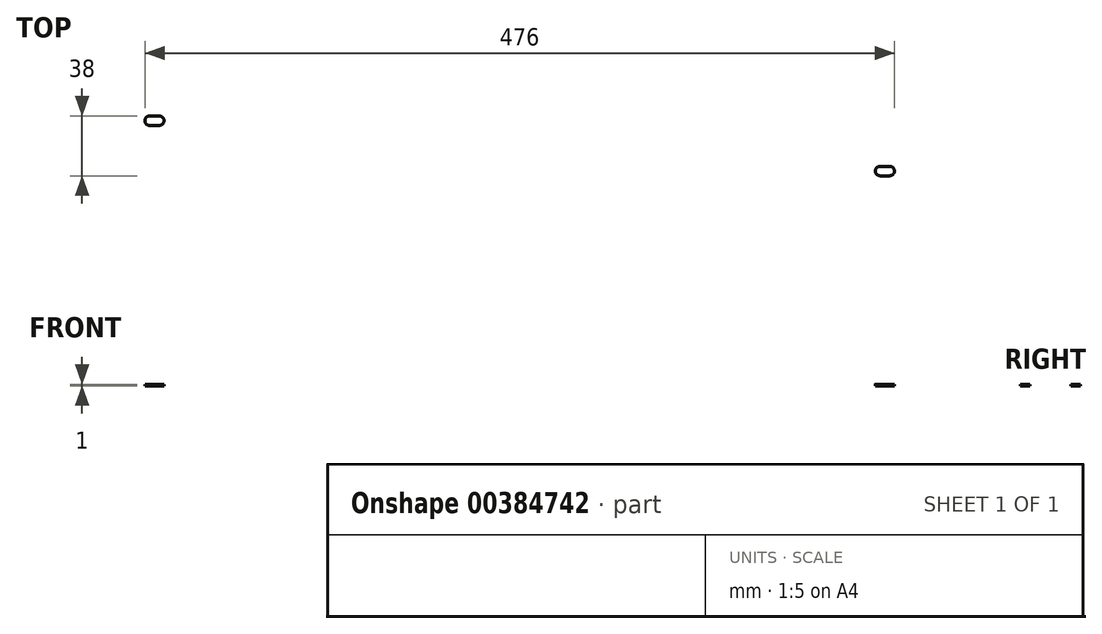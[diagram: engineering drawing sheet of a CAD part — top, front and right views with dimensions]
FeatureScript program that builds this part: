
annotation { "Feature Type Name" : "Feature", "Feature Type Description" : "" }
export const myFeature = defineFeature(function(context is Context, id is Id, definition is map)
    precondition{}
    {
        {
            var Q0;
            Q0=qCreatedBy(makeId("Top.planeOp"),FACE);
            var sketch = newSketch(context, id + "F0", { "sketchPlane" : qUnion([Q0])});
            skLineSegment(sketch, "E0.right", {"start": v(221, 33.5) * mm, "end": v(221, 20) * mm});
            skLineSegment(sketch, "E1", {"start": v(239, 22) * mm, "end": v(241, 20) * mm});
            skLineSegment(sketch, "E2", {"start": v(239, 22) * mm, "end": v(223, 22) * mm});
            skLineSegment(sketch, "E3", {"start": v(223, 22) * mm, "end": v(223, 20) * mm});
            skLineSegment(sketch, "E4", {"start": v(221, 20) * mm, "end": v(221, 33.5) * mm});
            skLineSegment(sketch, "E5", {"start": v(223, 20) * mm, "end": v(221, 20) * mm});
            skLineSegment(sketch, "E6", {"start": v(221, 33.5) * mm, "end": v(0, 33.5) * mm});
            skLineSegment(sketch, "E7", {"start": v(241, 20) * mm, "end": v(241, 0) * mm});
            skLineSegment(sketch, "E8.MirrorCS", {"start": v(-223, 20) * mm, "end": v(-221, 20) * mm});
            skLineSegment(sketch, "E9.MirrorCS", {"start": v(-223, 22) * mm, "end": v(-223, 20) * mm});
            skLineSegment(sketch, "E10.MirrorCS", {"start": v(-239, 22) * mm, "end": v(-241, 20) * mm});
            skLineSegment(sketch, "E11.MirrorCS", {"start": v(-221, 33.5) * mm, "end": v(-221, 20) * mm});
            skLineSegment(sketch, "E12.MirrorCS", {"start": v(-221, 33.5) * mm, "end": v(0, 33.5) * mm});
            skLineSegment(sketch, "E13.MirrorCS", {"start": v(-239, 22) * mm, "end": v(-223, 22) * mm});
            skLineSegment(sketch, "E14.MirrorCS", {"start": v(-241, 20) * mm, "end": v(-241, 0) * mm});
            skLineSegment(sketch, "E15.MirrorCS", {"start": v(-221, 20) * mm, "end": v(-221, 33.5) * mm});
            skLineSegment(sketch, "E16.MirrorCS", {"start": v(223, -22) * mm, "end": v(223, -20) * mm});
            skLineSegment(sketch, "E17.MirrorCS", {"start": v(-223, -22) * mm, "end": v(-223, -20) * mm});
            skLineSegment(sketch, "E18.MirrorCS", {"start": v(223, -20) * mm, "end": v(221, -20) * mm});
            skLineSegment(sketch, "E19.MirrorCS", {"start": v(-223, -20) * mm, "end": v(-221, -20) * mm});
            skLineSegment(sketch, "E20.MirrorCS", {"start": v(221, -20) * mm, "end": v(221, -33.5) * mm});
            skLineSegment(sketch, "E21.MirrorCS", {"start": v(-221, -33.5) * mm, "end": v(-221, -20) * mm});
            skLineSegment(sketch, "E22.MirrorCS", {"start": v(221, -33.5) * mm, "end": v(221, -20) * mm});
            skLineSegment(sketch, "E23.MirrorCS", {"start": v(-221, -20) * mm, "end": v(-221, -33.5) * mm});
            skLineSegment(sketch, "E24.MirrorCS", {"start": v(-239, -22) * mm, "end": v(-241, -20) * mm});
            skLineSegment(sketch, "E25.MirrorCS", {"start": v(-239, -22) * mm, "end": v(-223, -22) * mm});
            skLineSegment(sketch, "E26.MirrorCS", {"start": v(239, -22) * mm, "end": v(241, -20) * mm});
            skLineSegment(sketch, "E27.MirrorCS", {"start": v(239, -22) * mm, "end": v(223, -22) * mm});
            skLineSegment(sketch, "E28.MirrorCS", {"start": v(-241, -20) * mm, "end": v(-241, 0) * mm});
            skLineSegment(sketch, "E29.MirrorCS", {"start": v(241, -20) * mm, "end": v(241, 0) * mm});
            skLineSegment(sketch, "E30.MirrorCS", {"start": v(-221, -33.5) * mm, "end": v(0, -33.5) * mm});
            skLineSegment(sketch, "E31.MirrorCS", {"start": v(221, -33.5) * mm, "end": v(0, -33.5) * mm});
            skSolve(sketch);
        }
        {
            var Q0;
            Q0=makeQuery(id+"F0.imprint","IMPRINT",FACE,{"disambiguationData":[TD([[makeQuery(id+"F0.imprint","IMPRINT",EDGE,{"derivedFrom":sQuery(id+"F0.wireOp",EDGE,"E8.MirrorCS")}),-1.0]])]});
            extrude(context, id + "F1", {"entities" : qUnion([Q0]), "depth" : 1 * mm});
        }
        {
            var Q0;
            Q0=makeQuery(id+"F1.opExtrude","CAP_FACE",FACE,{"disambiguationData":[OSD([sQuery(id+"F0.wireOp",EDGE,"E8.MirrorCS"),sQuery(id+"F0.wireOp",EDGE,"E9.MirrorCS"),sQuery(id+"F0.wireOp",EDGE,"E11.MirrorCS"),sQuery(id+"F0.wireOp",EDGE,"E5"),sQuery(id+"F0.wireOp",EDGE,"E3"),sQuery(id+"F0.wireOp",EDGE,"E0.right"),sQuery(id+"F0.wireOp",EDGE,"E10.MirrorCS"),sQuery(id+"F0.wireOp",EDGE,"E2"),sQuery(id+"F0.wireOp",EDGE,"E13.MirrorCS"),sQuery(id+"F0.wireOp",EDGE,"E1"),sQuery(id+"F0.wireOp",EDGE,"E14.MirrorCS"),sQuery(id+"F0.wireOp",EDGE,"E7"),sQuery(id+"F0.wireOp",EDGE,"E6"),sQuery(id+"F0.wireOp",EDGE,"E12.MirrorCS"),sQuery(id+"F0.wireOp",EDGE,"E17.MirrorCS"),sQuery(id+"F0.wireOp",EDGE,"E16.MirrorCS"),sQuery(id+"F0.wireOp",EDGE,"E19.MirrorCS"),sQuery(id+"F0.wireOp",EDGE,"E18.MirrorCS"),sQuery(id+"F0.wireOp",EDGE,"E22.MirrorCS"),sQuery(id+"F0.wireOp",EDGE,"E23.MirrorCS"),sQuery(id+"F0.wireOp",EDGE,"E24.MirrorCS"),sQuery(id+"F0.wireOp",EDGE,"E25.MirrorCS"),sQuery(id+"F0.wireOp",EDGE,"E27.MirrorCS"),sQuery(id+"F0.wireOp",EDGE,"E26.MirrorCS"),sQuery(id+"F0.wireOp",EDGE,"E28.MirrorCS"),sQuery(id+"F0.wireOp",EDGE,"E29.MirrorCS"),sQuery(id+"F0.wireOp",EDGE,"E31.MirrorCS"),sQuery(id+"F0.wireOp",EDGE,"E30.MirrorCS")])],"isStart":false});
            var sketch = newSketch(context, id + "F2", { "sketchPlane" : qUnion([Q0])});
            skPoint(sketch, "E32", {"position": v(-200, 0) * mm});
            skPoint(sketch, "E33", {"position": v(-100, 0) * mm});
            skPoint(sketch, "E34", {"position": v(0, 0) * mm});
            skPoint(sketch, "E35", {"position": v(100, 0) * mm});
            skPoint(sketch, "E36", {"position": v(200, 0) * mm});
            skSolve(sketch);
        }
        {
            var Q0;
            Q0=sQuery(id+"F2.wireOp",VERTEX,"E32");
            var Q1;
            Q1=sQuery(id+"F2.wireOp",VERTEX,"E33");
            var Q2;
            Q2=sQuery(id+"F2.wireOp",VERTEX,"E34");
            var Q3;
            Q3=sQuery(id+"F2.wireOp",VERTEX,"E35");
            var Q4;
            Q4=sQuery(id+"F2.wireOp",VERTEX,"E36");
            var Q5;
            Q5=makeQuery(id+"F1.opExtrude","SWEPT_BODY",BODY,{"disambiguationData":[OSD([sQuery(id+"F0.wireOp",EDGE,"E8.MirrorCS"),sQuery(id+"F0.wireOp",EDGE,"E9.MirrorCS"),sQuery(id+"F0.wireOp",EDGE,"E11.MirrorCS"),sQuery(id+"F0.wireOp",EDGE,"E5"),sQuery(id+"F0.wireOp",EDGE,"E3"),sQuery(id+"F0.wireOp",EDGE,"E0.right"),sQuery(id+"F0.wireOp",EDGE,"E10.MirrorCS"),sQuery(id+"F0.wireOp",EDGE,"E2"),sQuery(id+"F0.wireOp",EDGE,"E13.MirrorCS"),sQuery(id+"F0.wireOp",EDGE,"E1"),sQuery(id+"F0.wireOp",EDGE,"E14.MirrorCS"),sQuery(id+"F0.wireOp",EDGE,"E7"),sQuery(id+"F0.wireOp",EDGE,"E6"),sQuery(id+"F0.wireOp",EDGE,"E12.MirrorCS"),sQuery(id+"F0.wireOp",EDGE,"E17.MirrorCS"),sQuery(id+"F0.wireOp",EDGE,"E16.MirrorCS"),sQuery(id+"F0.wireOp",EDGE,"E19.MirrorCS"),sQuery(id+"F0.wireOp",EDGE,"E18.MirrorCS"),sQuery(id+"F0.wireOp",EDGE,"E22.MirrorCS"),sQuery(id+"F0.wireOp",EDGE,"E23.MirrorCS"),sQuery(id+"F0.wireOp",EDGE,"E24.MirrorCS"),sQuery(id+"F0.wireOp",EDGE,"E25.MirrorCS"),sQuery(id+"F0.wireOp",EDGE,"E27.MirrorCS"),sQuery(id+"F0.wireOp",EDGE,"E26.MirrorCS"),sQuery(id+"F0.wireOp",EDGE,"E28.MirrorCS"),sQuery(id+"F0.wireOp",EDGE,"E29.MirrorCS"),sQuery(id+"F0.wireOp",EDGE,"E31.MirrorCS"),sQuery(id+"F0.wireOp",EDGE,"E30.MirrorCS")])]});
            hole(context, id + "F3", {"style" : HoleStyle.SIMPLE, "endStyle" : HoleEndStyle.THROUGH, "holeDiameter" : 5 * mm, "isTappedThrough" : true, "tappedDepth" : 12 * mm, "tapClearance" : 3, "locations" : qUnion([Q0, Q1, Q2, Q3, Q4]), "scope" : qUnion([Q5])});
        }
        {
            var Q0;
            Q0=makeQuery(id+"F1.opExtrude","CAP_FACE",FACE,{"disambiguationData":[OSD([sQuery(id+"F0.wireOp",EDGE,"E8.MirrorCS"),sQuery(id+"F0.wireOp",EDGE,"E9.MirrorCS"),sQuery(id+"F0.wireOp",EDGE,"E11.MirrorCS"),sQuery(id+"F0.wireOp",EDGE,"E5"),sQuery(id+"F0.wireOp",EDGE,"E3"),sQuery(id+"F0.wireOp",EDGE,"E0.right"),sQuery(id+"F0.wireOp",EDGE,"E10.MirrorCS"),sQuery(id+"F0.wireOp",EDGE,"E2"),sQuery(id+"F0.wireOp",EDGE,"E13.MirrorCS"),sQuery(id+"F0.wireOp",EDGE,"E1"),sQuery(id+"F0.wireOp",EDGE,"E14.MirrorCS"),sQuery(id+"F0.wireOp",EDGE,"E7"),sQuery(id+"F0.wireOp",EDGE,"E6"),sQuery(id+"F0.wireOp",EDGE,"E12.MirrorCS"),sQuery(id+"F0.wireOp",EDGE,"E17.MirrorCS"),sQuery(id+"F0.wireOp",EDGE,"E16.MirrorCS"),sQuery(id+"F0.wireOp",EDGE,"E19.MirrorCS"),sQuery(id+"F0.wireOp",EDGE,"E18.MirrorCS"),sQuery(id+"F0.wireOp",EDGE,"E22.MirrorCS"),sQuery(id+"F0.wireOp",EDGE,"E23.MirrorCS"),sQuery(id+"F0.wireOp",EDGE,"E24.MirrorCS"),sQuery(id+"F0.wireOp",EDGE,"E25.MirrorCS"),sQuery(id+"F0.wireOp",EDGE,"E27.MirrorCS"),sQuery(id+"F0.wireOp",EDGE,"E26.MirrorCS"),sQuery(id+"F0.wireOp",EDGE,"E28.MirrorCS"),sQuery(id+"F0.wireOp",EDGE,"E29.MirrorCS"),sQuery(id+"F0.wireOp",EDGE,"E31.MirrorCS"),sQuery(id+"F0.wireOp",EDGE,"E30.MirrorCS")])],"isStart":false});
            var sketch = newSketch(context, id + "F4", { "sketchPlane" : qUnion([Q0])});
            skPoint(sketch, "E37.MirrorP", {"position": v(-228.9, -16) * mm});
            skPoint(sketch, "E38.MirrorP", {"position": v(-235, -16) * mm});
            skArc(sketch, "E39", {"start": v(-235, -13) * mm, "mid": v(-238, -16) * mm, "end": v(-235, -19) * mm});
            skArc(sketch, "E40", {"start": v(-228.9, -19) * mm, "mid": v(-225.9, -16) * mm, "end": v(-228.9, -13) * mm});
            skLineSegment(sketch, "E41", {"start": v(-235, -13) * mm, "end": v(-228.9, -13) * mm});
            skLineSegment(sketch, "E42", {"start": v(-228.9, -19) * mm, "end": v(-235, -19) * mm});
            skPoint(sketch, "E43.MirrorP", {"position": v(235, -16) * mm});
            skPoint(sketch, "E44.MirrorP", {"position": v(228.9, -16) * mm});
            skArc(sketch, "E45.MirrorCS", {"start": v(228.9, -19) * mm, "mid": v(225.9, -16) * mm, "end": v(228.9, -13) * mm});
            skLineSegment(sketch, "E46.MirrorCS", {"start": v(235, -13) * mm, "end": v(228.9, -13) * mm});
            skLineSegment(sketch, "E47.MirrorCS", {"start": v(228.9, -19) * mm, "end": v(235, -19) * mm});
            skArc(sketch, "E48.MirrorCS", {"start": v(235, -13) * mm, "mid": v(238, -16) * mm, "end": v(235, -19) * mm});
            skArc(sketch, "E49.MirrorCS", {"start": v(-235, 13) * mm, "mid": v(-238, 16) * mm, "end": v(-235, 19) * mm});
            skLineSegment(sketch, "E50.MirrorCS", {"start": v(-235, 13) * mm, "end": v(-228.9, 13) * mm});
            skArc(sketch, "E51.MirrorCS", {"start": v(-228.9, 19) * mm, "mid": v(-225.9, 16) * mm, "end": v(-228.9, 13) * mm});
            skLineSegment(sketch, "E52.MirrorCS", {"start": v(-228.9, 19) * mm, "end": v(-235, 19) * mm});
            skLineSegment(sketch, "E53.MirrorCS", {"start": v(235, 13) * mm, "end": v(228.9, 13) * mm});
            skLineSegment(sketch, "E54.MirrorCS", {"start": v(228.9, 19) * mm, "end": v(235, 19) * mm});
            skArc(sketch, "E55.MirrorCS", {"start": v(228.9, 19) * mm, "mid": v(225.9, 16) * mm, "end": v(228.9, 13) * mm});
            skArc(sketch, "E56.MirrorCS", {"start": v(235, 13) * mm, "mid": v(238, 16) * mm, "end": v(235, 19) * mm});
            skSolve(sketch);
        }
        {
            var Q0;
            Q0=makeQuery(id+"F4.imprint","IMPRINT",FACE,{"disambiguationData":[TD([[makeQuery(id+"F4.imprint","IMPRINT",EDGE,{"derivedFrom":sQuery(id+"F4.wireOp",EDGE,"E39")}),1.0]])]});
            var Q1;
            Q1=makeQuery(id+"F4.imprint","IMPRINT",FACE,{"disambiguationData":[TD([[makeQuery(id+"F4.imprint","IMPRINT",EDGE,{"derivedFrom":sQuery(id+"F4.wireOp",EDGE,"E49.MirrorCS")}),-1.0]])]});
            var Q2;
            Q2=makeQuery(id+"F4.imprint","IMPRINT",FACE,{"disambiguationData":[TD([[makeQuery(id+"F4.imprint","IMPRINT",EDGE,{"derivedFrom":sQuery(id+"F4.wireOp",EDGE,"E53.MirrorCS")}),-1.0]])]});
            var Q3;
            Q3=makeQuery(id+"F4.imprint","IMPRINT",FACE,{"disambiguationData":[TD([[makeQuery(id+"F4.imprint","IMPRINT",EDGE,{"derivedFrom":sQuery(id+"F4.wireOp",EDGE,"E45.MirrorCS")}),-1.0]])]});
            extrude(context, id + "F5", {"entities" : qUnion([Q0, Q1, Q2, Q3]), "operationType" : NewBodyOperationType.REMOVE, "oppositeDirection" : true, "depth" : 25 * mm});
        }
        {
            var Q0;
            Q0=makeQuery(id+"F1.opExtrude","CAP_FACE",FACE,{"disambiguationData":[OSD([sQuery(id+"F0.wireOp",EDGE,"E8.MirrorCS"),sQuery(id+"F0.wireOp",EDGE,"E9.MirrorCS"),sQuery(id+"F0.wireOp",EDGE,"E11.MirrorCS"),sQuery(id+"F0.wireOp",EDGE,"E5"),sQuery(id+"F0.wireOp",EDGE,"E3"),sQuery(id+"F0.wireOp",EDGE,"E0.right"),sQuery(id+"F0.wireOp",EDGE,"E10.MirrorCS"),sQuery(id+"F0.wireOp",EDGE,"E2"),sQuery(id+"F0.wireOp",EDGE,"E13.MirrorCS"),sQuery(id+"F0.wireOp",EDGE,"E1"),sQuery(id+"F0.wireOp",EDGE,"E14.MirrorCS"),sQuery(id+"F0.wireOp",EDGE,"E7"),sQuery(id+"F0.wireOp",EDGE,"E6"),sQuery(id+"F0.wireOp",EDGE,"E12.MirrorCS"),sQuery(id+"F0.wireOp",EDGE,"E17.MirrorCS"),sQuery(id+"F0.wireOp",EDGE,"E16.MirrorCS"),sQuery(id+"F0.wireOp",EDGE,"E19.MirrorCS"),sQuery(id+"F0.wireOp",EDGE,"E18.MirrorCS"),sQuery(id+"F0.wireOp",EDGE,"E22.MirrorCS"),sQuery(id+"F0.wireOp",EDGE,"E23.MirrorCS"),sQuery(id+"F0.wireOp",EDGE,"E24.MirrorCS"),sQuery(id+"F0.wireOp",EDGE,"E25.MirrorCS"),sQuery(id+"F0.wireOp",EDGE,"E27.MirrorCS"),sQuery(id+"F0.wireOp",EDGE,"E26.MirrorCS"),sQuery(id+"F0.wireOp",EDGE,"E28.MirrorCS"),sQuery(id+"F0.wireOp",EDGE,"E29.MirrorCS"),sQuery(id+"F0.wireOp",EDGE,"E31.MirrorCS"),sQuery(id+"F0.wireOp",EDGE,"E30.MirrorCS")])],"isStart":true});
            var sketch = newSketch(context, id + "F6", { "sketchPlane" : qUnion([Q0])});
            skLineSegment(sketch, "E57.bottom", {"start": v(-120, 12) * mm, "end": v(-180, 12) * mm});
            skLineSegment(sketch, "E57.top", {"start": v(-120, -12) * mm, "end": v(-180, -12) * mm});
            skLineSegment(sketch, "E57.left", {"start": v(-115, 7) * mm, "end": v(-115, -7) * mm});
            skLineSegment(sketch, "E57.right", {"start": v(-185, 7) * mm, "end": v(-185, -7) * mm});
            skPoint(sketch, "E57.middle", {"position": v(-150, 0) * mm});
            skPoint(sketch, "E58.visualSharp", {"position": v(-115, 12) * mm});
            skArc(sketch, "E58.filletArc", {"start": v(-115, 7) * mm, "mid": v(-116.46, 10.54) * mm, "end": v(-120, 12) * mm});
            skPoint(sketch, "E59.visualSharp", {"position": v(-185, 12) * mm});
            skArc(sketch, "E59.filletArc", {"start": v(-180, 12) * mm, "mid": v(-183.54, 10.54) * mm, "end": v(-185, 7) * mm});
            skPoint(sketch, "E60.visualSharp", {"position": v(-185, -12) * mm});
            skArc(sketch, "E60.filletArc", {"start": v(-185, -7) * mm, "mid": v(-183.54, -10.54) * mm, "end": v(-180, -12) * mm});
            skPoint(sketch, "E61.visualSharp", {"position": v(-115, -12) * mm});
            skArc(sketch, "E61.filletArc", {"start": v(-120, -12) * mm, "mid": v(-116.46, -10.54) * mm, "end": v(-115, -7) * mm});
            skLineSegment(sketch, "E62.bottom", {"start": v(-20, 12) * mm, "end": v(-80, 12) * mm});
            skLineSegment(sketch, "E62.top", {"start": v(-20, -12) * mm, "end": v(-80, -12) * mm});
            skLineSegment(sketch, "E62.left", {"start": v(-15, 7) * mm, "end": v(-15, -7) * mm});
            skLineSegment(sketch, "E62.right", {"start": v(-85, 7) * mm, "end": v(-85, -7) * mm});
            skPoint(sketch, "E62.middle", {"position": v(-50, 0) * mm});
            skPoint(sketch, "E63.visualSharp", {"position": v(-15, 12) * mm});
            skArc(sketch, "E63.filletArc", {"start": v(-15, 7) * mm, "mid": v(-16.46, 10.54) * mm, "end": v(-20, 12) * mm});
            skPoint(sketch, "E64.visualSharp", {"position": v(-85, 12) * mm});
            skArc(sketch, "E64.filletArc", {"start": v(-80, 12) * mm, "mid": v(-83.54, 10.54) * mm, "end": v(-85, 7) * mm});
            skPoint(sketch, "E65.visualSharp", {"position": v(-85, -12) * mm});
            skArc(sketch, "E65.filletArc", {"start": v(-85, -7) * mm, "mid": v(-83.54, -10.54) * mm, "end": v(-80, -12) * mm});
            skPoint(sketch, "E66.visualSharp", {"position": v(-15, -12) * mm});
            skArc(sketch, "E66.filletArc", {"start": v(-20, -12) * mm, "mid": v(-16.46, -10.54) * mm, "end": v(-15, -7) * mm});
            skArc(sketch, "E67.MirrorCS", {"start": v(15, 7) * mm, "mid": v(16.46, 10.54) * mm, "end": v(20, 12) * mm});
            skArc(sketch, "E68.MirrorCS", {"start": v(80, 12) * mm, "mid": v(83.54, 10.54) * mm, "end": v(85, 7) * mm});
            skArc(sketch, "E69.MirrorCS", {"start": v(85, -7) * mm, "mid": v(83.54, -10.54) * mm, "end": v(80, -12) * mm});
            skArc(sketch, "E70.MirrorCS", {"start": v(20, -12) * mm, "mid": v(16.46, -10.54) * mm, "end": v(15, -7) * mm});
            skArc(sketch, "E71.MirrorCS", {"start": v(115, 7) * mm, "mid": v(116.46, 10.54) * mm, "end": v(120, 12) * mm});
            skArc(sketch, "E72.MirrorCS", {"start": v(180, 12) * mm, "mid": v(183.54, 10.54) * mm, "end": v(185, 7) * mm});
            skArc(sketch, "E73.MirrorCS", {"start": v(185, -7) * mm, "mid": v(183.54, -10.54) * mm, "end": v(180, -12) * mm});
            skArc(sketch, "E74.MirrorCS", {"start": v(120, -12) * mm, "mid": v(116.46, -10.54) * mm, "end": v(115, -7) * mm});
            skPoint(sketch, "E75.MirrorP", {"position": v(185, 12) * mm});
            skPoint(sketch, "E76.MirrorP", {"position": v(150, 0) * mm});
            skPoint(sketch, "E77.MirrorP", {"position": v(15, -12) * mm});
            skPoint(sketch, "E78.MirrorP", {"position": v(15, 12) * mm});
            skPoint(sketch, "E79.MirrorP", {"position": v(115, -12) * mm});
            skPoint(sketch, "E80.MirrorP", {"position": v(115, 12) * mm});
            skPoint(sketch, "E81.MirrorP", {"position": v(50, 0) * mm});
            skPoint(sketch, "E82.MirrorP", {"position": v(85, 12) * mm});
            skPoint(sketch, "E83.MirrorP", {"position": v(85, -12) * mm});
            skLineSegment(sketch, "E84.MirrorCS", {"start": v(85, 7) * mm, "end": v(85, -7) * mm});
            skLineSegment(sketch, "E85.MirrorCS", {"start": v(15, 7) * mm, "end": v(15, -7) * mm});
            skLineSegment(sketch, "E86.MirrorCS", {"start": v(120, 12) * mm, "end": v(180, 12) * mm});
            skLineSegment(sketch, "E87.MirrorCS", {"start": v(120, -12) * mm, "end": v(180, -12) * mm});
            skLineSegment(sketch, "E88.MirrorCS", {"start": v(115, 7) * mm, "end": v(115, -7) * mm});
            skLineSegment(sketch, "E89.MirrorCS", {"start": v(185, 7) * mm, "end": v(185, -7) * mm});
            skPoint(sketch, "E90.MirrorP", {"position": v(185, -12) * mm});
            skLineSegment(sketch, "E91.MirrorCS", {"start": v(20, 12) * mm, "end": v(80, 12) * mm});
            skLineSegment(sketch, "E92.MirrorCS", {"start": v(20, -12) * mm, "end": v(80, -12) * mm});
            skSolve(sketch);
        }
        {
            var Q0;
            Q0=makeQuery(id+"F6.imprint","IMPRINT",FACE,{"disambiguationData":[TD([[makeQuery(id+"F6.imprint","IMPRINT",EDGE,{"derivedFrom":sQuery(id+"F6.wireOp",EDGE,"E71.MirrorCS")}),-1.0]])]});
            var Q1;
            Q1=makeQuery(id+"F6.imprint","IMPRINT",FACE,{"disambiguationData":[TD([[makeQuery(id+"F6.imprint","IMPRINT",EDGE,{"derivedFrom":sQuery(id+"F6.wireOp",EDGE,"E67.MirrorCS")}),-1.0]])]});
            var Q2;
            Q2=makeQuery(id+"F6.imprint","IMPRINT",FACE,{"disambiguationData":[TD([[makeQuery(id+"F6.imprint","IMPRINT",EDGE,{"derivedFrom":sQuery(id+"F6.wireOp",EDGE,"E62.bottom")}),1.0]])]});
            var Q3;
            Q3=makeQuery(id+"F6.imprint","IMPRINT",FACE,{"disambiguationData":[TD([[makeQuery(id+"F6.imprint","IMPRINT",EDGE,{"derivedFrom":sQuery(id+"F6.wireOp",EDGE,"E57.bottom")}),1.0]])]});
            extrude(context, id + "F7", {"entities" : qUnion([Q0, Q1, Q2, Q3]), "operationType" : NewBodyOperationType.REMOVE, "oppositeDirection" : true, "depth" : 25 * mm, "offsetDistance" : 25 * mm});
        }
    });
